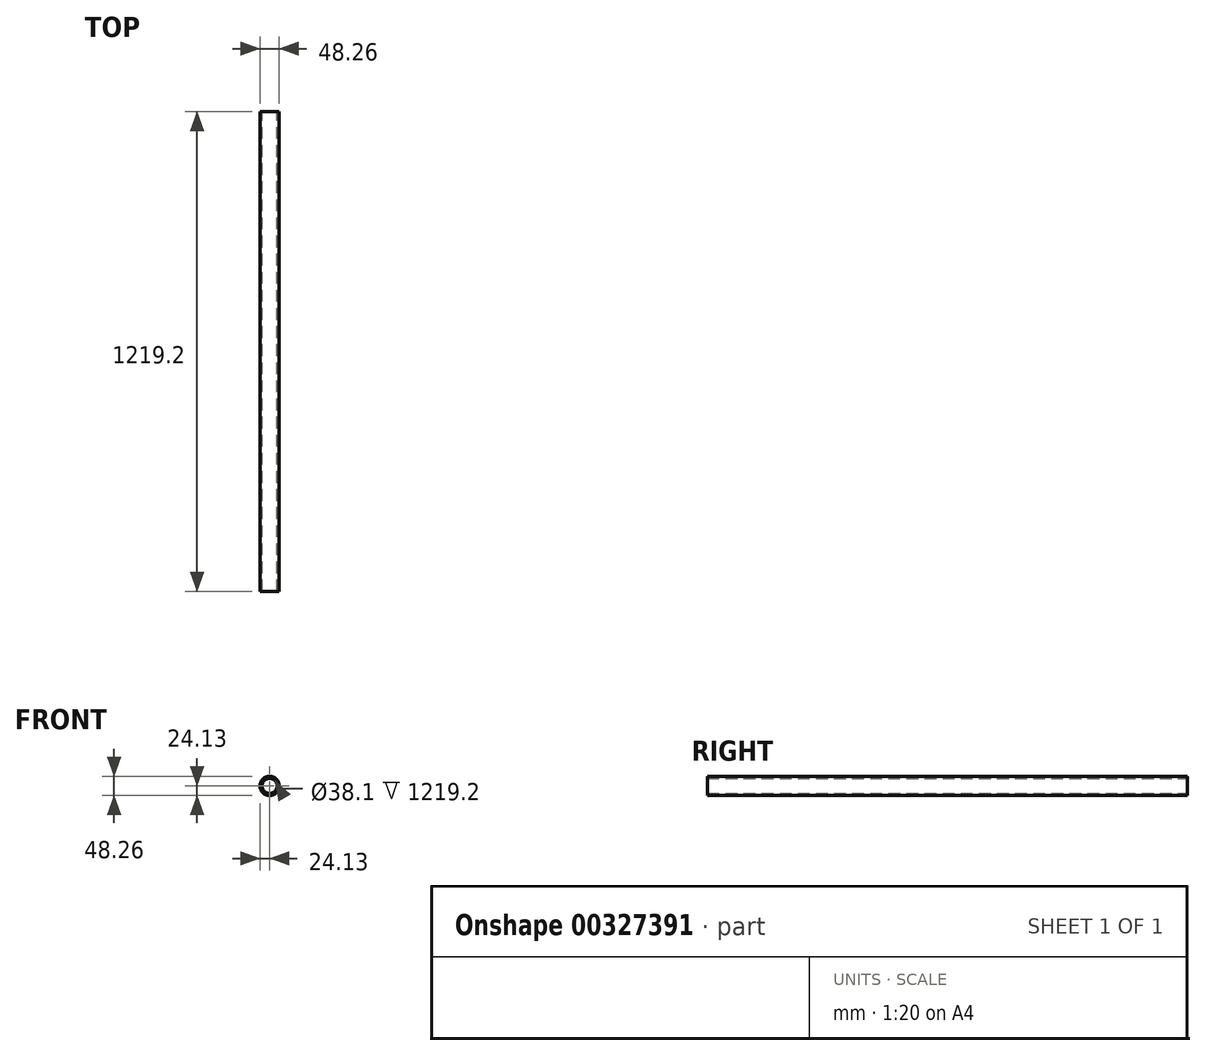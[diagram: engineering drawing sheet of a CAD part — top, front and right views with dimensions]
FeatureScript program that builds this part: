
annotation { "Feature Type Name" : "Feature", "Feature Type Description" : "" }
export const myFeature = defineFeature(function(context is Context, id is Id, definition is map)
    precondition{}
    {
        {
            var Q0;
            Q0=qCreatedBy(makeId("Front.planeOp"), FACE);
            var sketch = newSketch(context, id + "F0", { "sketchPlane" : qUnion([Q0])});
            skCircle(sketch, "E0", {"center": v(0, 0) * mm, "radius": 24.13 * mm});
            skCircle(sketch, "E1", {"center": v(0, 0) * mm, "radius": 19.05 * mm});
            skSolve(sketch);
        }
        {
            var Q0;
            Q0 = qSketchRegion(id + "F0", true);
            extrude(context, id + "F1", {"entities" : qUnion([Q0]), "depth" : 1219.2 * mm, "offsetDistance" : 25.4 * mm, "symmetric" : true});
        }
    });
